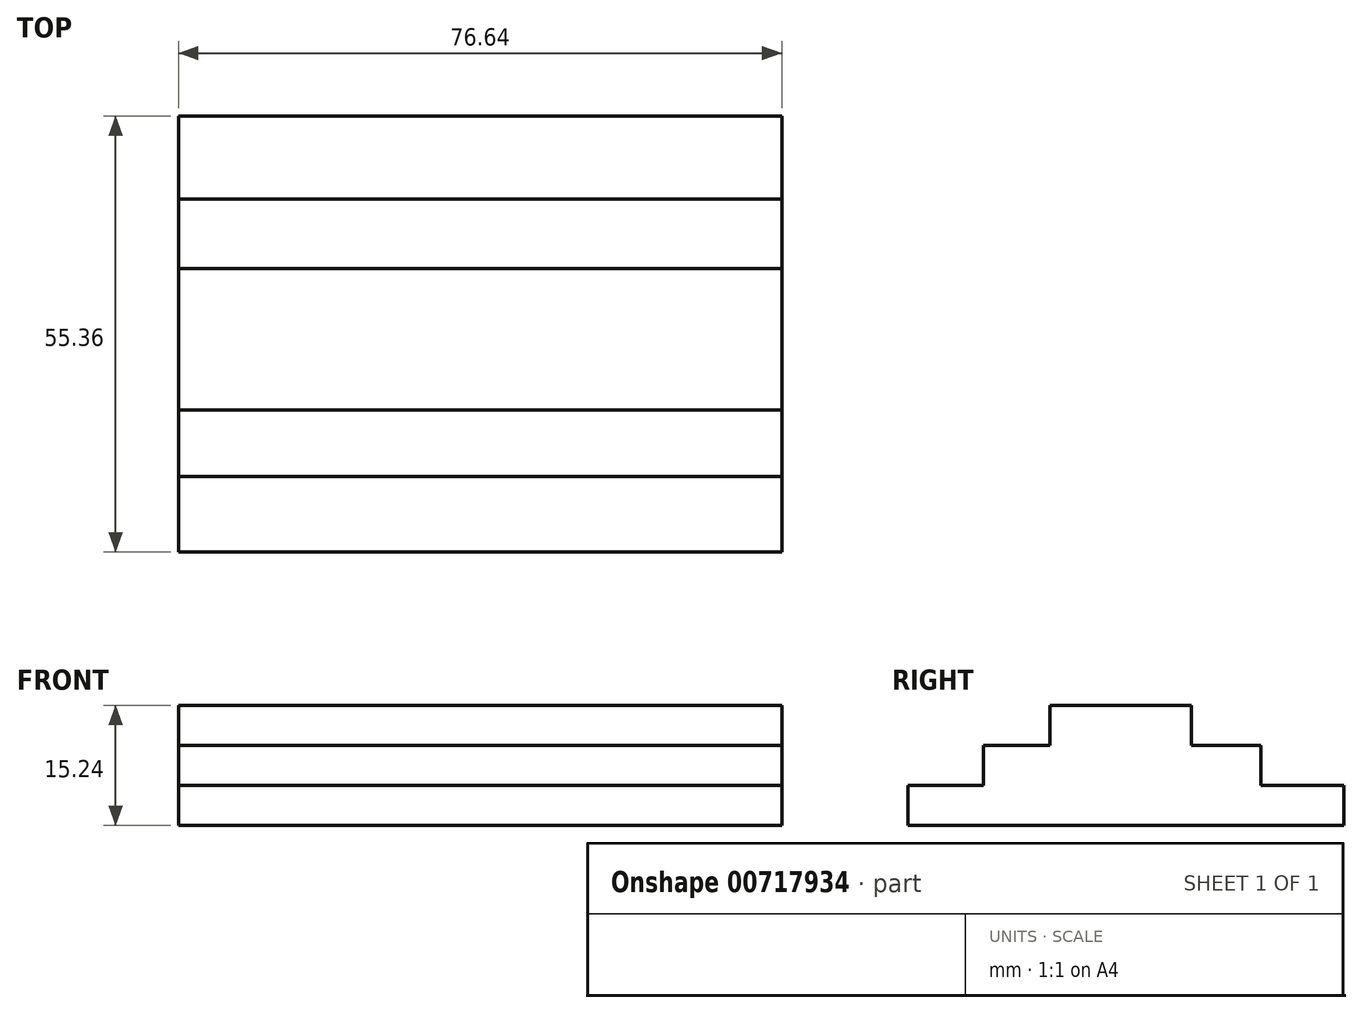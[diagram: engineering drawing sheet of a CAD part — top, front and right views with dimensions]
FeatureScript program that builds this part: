
annotation { "Feature Type Name" : "Feature", "Feature Type Description" : "" }
export const myFeature = defineFeature(function(context is Context, id is Id, definition is map)
    precondition{}
    {
        {
            var Q0;
            Q0=qCreatedBy(makeId("Top.planeOp"),FACE);
            var sketch = newSketch(context, id + "F0", { "sketchPlane" : qUnion([Q0])});
            skLineSegment(sketch, "E0.bottom", {"start": v(-38.4, 25.8) * mm, "end": v(38.24, 25.8) * mm});
            skLineSegment(sketch, "E0.top", {"start": v(-38.4, -29.56) * mm, "end": v(38.24, -29.56) * mm});
            skLineSegment(sketch, "E0.left", {"start": v(-38.4, 25.8) * mm, "end": v(-38.4, -29.56) * mm});
            skLineSegment(sketch, "E0.right", {"start": v(38.24, 25.8) * mm, "end": v(38.24, -29.56) * mm});
            skSolve(sketch);
        }
        {
            var Q0;
            Q0=makeQuery(id+"F0.imprint","IMPRINT",FACE,{"disambiguationData":[TD([[makeQuery(id+"F0.imprint","IMPRINT",EDGE,{"derivedFrom":sQuery(id+"F0.wireOp",EDGE,"E0.bottom")}),-1.0]])]});
            extrude(context, id + "F1", {"entities" : qUnion([Q0]), "depth" : 25.4 * mm, "offsetDistance" : 25.4 * mm});
        }
        {
            var Q0;
            Q0=makeQuery(id+"F1.opExtrude","CAP_FACE",FACE,{"disambiguationData":[OSD([sQuery(id+"F0.wireOp",EDGE,"E0.bottom"),sQuery(id+"F0.wireOp",EDGE,"E0.top"),sQuery(id+"F0.wireOp",EDGE,"E0.left"),sQuery(id+"F0.wireOp",EDGE,"E0.right")])],"isStart":false});
            var sketch = newSketch(context, id + "F2", { "sketchPlane" : qUnion([Q0])});
            skLineSegment(sketch, "E1", {"start": v(-38.4, -19.96) * mm, "end": v(38.24, -19.96) * mm});
            skLineSegment(sketch, "E2", {"start": v(-38.4, -11.54) * mm, "end": v(38.24, -11.54) * mm});
            skLineSegment(sketch, "E3", {"start": v(-38.4, -1.88) * mm, "end": v(38.24, -1.88) * mm});
            skLineSegment(sketch, "E4", {"start": v(-38.4, 6.47) * mm, "end": v(38.24, 6.47) * mm});
            skLineSegment(sketch, "E5", {"start": v(-38.4, 15.28) * mm, "end": v(38.24, 15.28) * mm});
            skSolve(sketch);
        }
        {
            var Q0;
            {var subQ0=sQuery(id+"F2.wireOp",EDGE,"E1");Q0=makeQuery(id+"F2.imprint","IMPRINT",FACE,{"disambiguationData":[TD([[makeQuery(id+"F2.imprint","IMPRINT",EDGE,{"derivedFrom":subQ0}),-1.0]])]});}
            extrude(context, id + "F3", {"entities" : qUnion([Q0]), "operationType" : NewBodyOperationType.REMOVE, "oppositeDirection" : true, "depth" : 20.32 * mm, "offsetDistance" : 25.4 * mm});
        }
        {
            var Q0;
            {var subQ0=sQuery(id+"F2.wireOp",EDGE,"E1");Q0=makeQuery(id+"F2.imprint","IMPRINT",FACE,{"disambiguationData":[TD([[makeQuery(id+"F2.imprint","IMPRINT",EDGE,{"derivedFrom":subQ0}),1.0]])]});}
            extrude(context, id + "F4", {"entities" : qUnion([Q0]), "operationType" : NewBodyOperationType.REMOVE, "oppositeDirection" : true, "depth" : 15.24 * mm, "offsetDistance" : 25.4 * mm});
        }
        {
            var Q0;
            {var subQ0=sQuery(id+"F2.wireOp",EDGE,"E2");Q0=makeQuery(id+"F2.imprint","IMPRINT",FACE,{"disambiguationData":[TD([[makeQuery(id+"F2.imprint","IMPRINT",EDGE,{"derivedFrom":subQ0}),1.0]])]});}
            extrude(context, id + "F5", {"entities" : qUnion([Q0]), "operationType" : NewBodyOperationType.REMOVE, "oppositeDirection" : true, "depth" : 10.16 * mm, "offsetDistance" : 25.4 * mm});
        }
        {
            var Q0;
            {var subQ0=sQuery(id+"F2.wireOp",EDGE,"E3");Q0=makeQuery(id+"F2.imprint","IMPRINT",FACE,{"disambiguationData":[TD([[makeQuery(id+"F2.imprint","IMPRINT",EDGE,{"derivedFrom":subQ0}),1.0]])]});}
            extrude(context, id + "F6", {"entities" : qUnion([Q0]), "operationType" : NewBodyOperationType.REMOVE, "oppositeDirection" : true, "depth" : 10.16 * mm, "offsetDistance" : 25.4 * mm});
        }
        {
            var Q0;
            {var subQ0=sQuery(id+"F2.wireOp",EDGE,"E4");Q0=makeQuery(id+"F2.imprint","IMPRINT",FACE,{"disambiguationData":[TD([[makeQuery(id+"F2.imprint","IMPRINT",EDGE,{"derivedFrom":subQ0}),1.0]])]});}
            extrude(context, id + "F7", {"entities" : qUnion([Q0]), "operationType" : NewBodyOperationType.REMOVE, "oppositeDirection" : true, "depth" : 15.24 * mm, "offsetDistance" : 25.4 * mm});
        }
        {
            var Q0;
            {var subQ0=sQuery(id+"F2.wireOp",EDGE,"E5");Q0=makeQuery(id+"F2.imprint","IMPRINT",FACE,{"disambiguationData":[TD([[makeQuery(id+"F2.imprint","IMPRINT",EDGE,{"derivedFrom":subQ0}),1.0]])]});}
            extrude(context, id + "F8", {"entities" : qUnion([Q0]), "operationType" : NewBodyOperationType.REMOVE, "oppositeDirection" : true, "depth" : 20.32 * mm, "offsetDistance" : 25.4 * mm});
        }
    });
